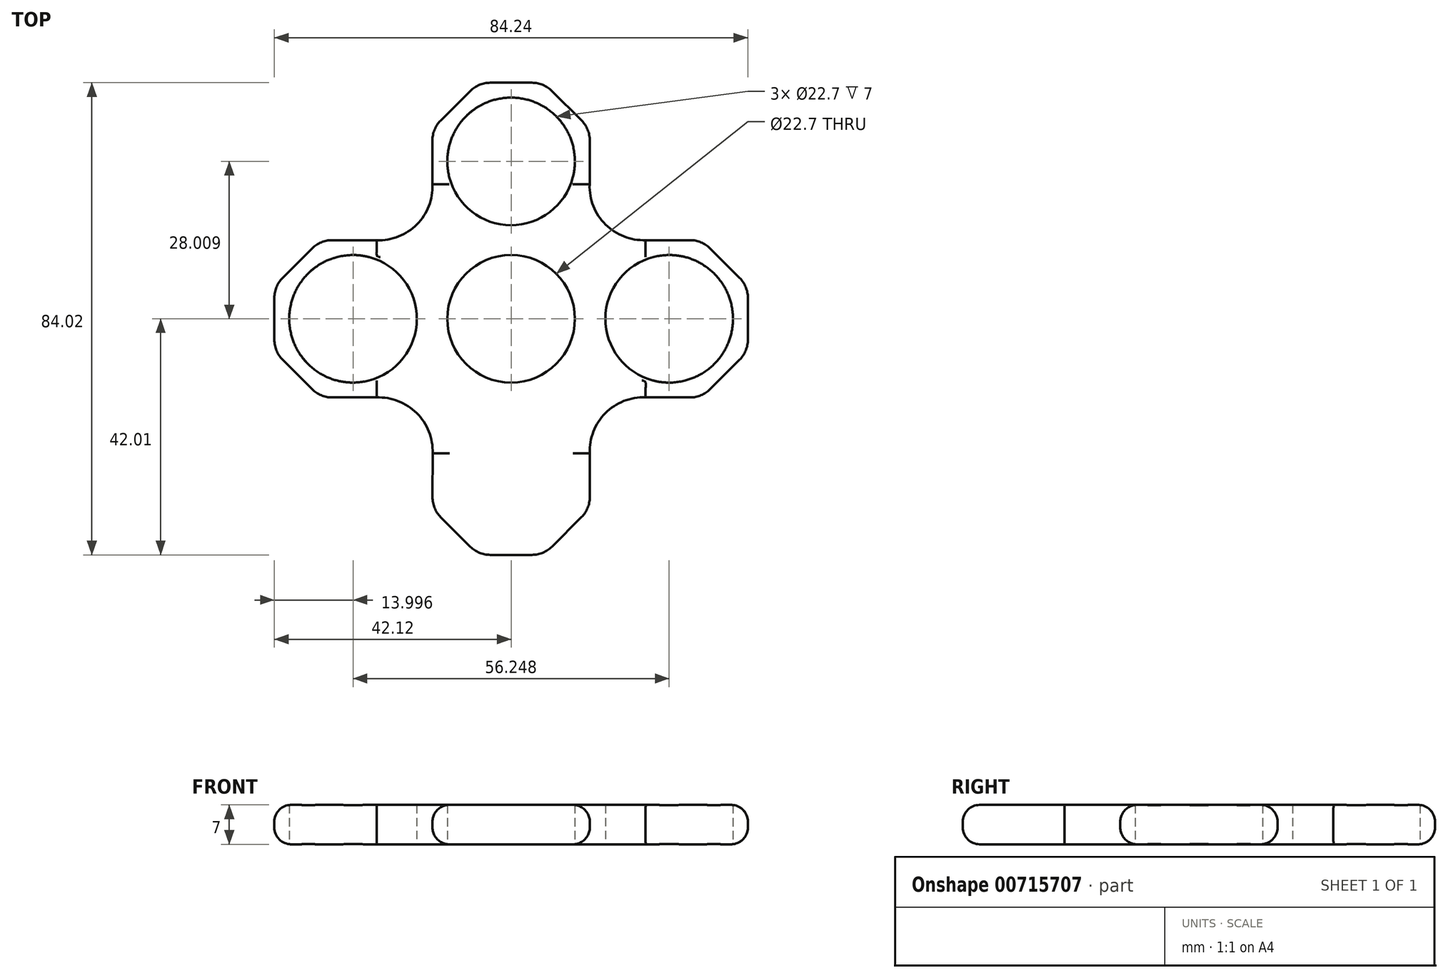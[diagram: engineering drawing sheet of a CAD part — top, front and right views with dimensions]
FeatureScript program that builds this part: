
annotation { "Feature Type Name" : "Feature", "Feature Type Description" : "" }
export const myFeature = defineFeature(function(context is Context, id is Id, definition is map)
    precondition{}
    {
        {
            var Q0;
            Q0=qCreatedBy(makeId("Top.planeOp"),FACE);
            var sketch = newSketch(context, id + "F0", { "sketchPlane" : qUnion([Q0])});
            skCircle(sketch, "E0", {"center": v(0, 0) * mm, "radius": 11.35 * mm});
            skCircle(sketch, "E1", {"center": v(28.12, 0) * mm, "radius": 11.35 * mm});
            skLineSegment(sketch, "E2.1", {"start": v(35.39, 12.54) * mm, "end": v(40.66, 7.26) * mm});
            skLineSegment(sketch, "E2.2", {"start": v(42.12, 3.73) * mm, "end": v(42.12, -3.73) * mm});
            skLineSegment(sketch, "E3.MirrorCS", {"start": v(-42.12, 3.73) * mm, "end": v(-42.12, -3.73) * mm});
            skLineSegment(sketch, "E4.MirrorCS", {"start": v(-40.66, -7.26) * mm, "end": v(-35.39, -12.54) * mm});
            skCircle(sketch, "E5.MirrorC", {"center": v(-28.12, 0) * mm, "radius": 11.35 * mm});
            skCircle(sketch, "E6", {"center": v(0, 28) * mm, "radius": 11.35 * mm});
            skLineSegment(sketch, "E7.0", {"start": v(-3.73, 42) * mm, "end": v(3.73, 42) * mm});
            skLineSegment(sketch, "E7.7", {"start": v(-12.54, 35.27) * mm, "end": v(-7.26, 40.54) * mm});
            skCircle(sketch, "E8.MirrorC", {"center": v(0, -28) * mm, "radius": 11.35 * mm});
            skLineSegment(sketch, "E9.MirrorCS", {"start": v(7.26, -40.54) * mm, "end": v(12.54, -35.27) * mm});
            skLineSegment(sketch, "E10.MirrorCS", {"start": v(-3.73, -42) * mm, "end": v(3.73, -42) * mm});
            skLineSegment(sketch, "E11", {"start": v(-35.4, 12.53) * mm, "end": v(-40.66, 7.26) * mm});
            skLineSegment(sketch, "E12", {"start": v(7.26, 40.54) * mm, "end": v(12.53, 35.28) * mm});
            skLineSegment(sketch, "E13", {"start": v(40.66, -7.26) * mm, "end": v(35.4, -12.53) * mm});
            skLineSegment(sketch, "E14", {"start": v(-7.26, -40.54) * mm, "end": v(-12.53, -35.28) * mm});
            skArc(sketch, "E15", {"start": v(13.97, 23.9) * mm, "mid": v(16.8, 16.78) * mm, "end": v(23.93, 14) * mm});
            skArc(sketch, "E16.1.0", {"start": v(-23.9, 13.97) * mm, "mid": v(-16.78, 16.8) * mm, "end": v(-14, 23.93) * mm});
            skArc(sketch, "E16.2.0", {"start": v(-13.97, -23.9) * mm, "mid": v(-16.8, -16.78) * mm, "end": v(-23.93, -14) * mm});
            skArc(sketch, "E16.3.0", {"start": v(23.9, -13.97) * mm, "mid": v(16.78, -16.8) * mm, "end": v(14, -23.93) * mm});
            skLineSegment(sketch, "E17", {"start": v(-14, 31.74) * mm, "end": v(-14, 23.93) * mm});
            skLineSegment(sketch, "E18", {"start": v(14, 31.73) * mm, "end": v(13.97, 23.9) * mm});
            skLineSegment(sketch, "E19", {"start": v(31.85, 14) * mm, "end": v(23.93, 14) * mm});
            skLineSegment(sketch, "E20", {"start": v(31.84, -14) * mm, "end": v(23.9, -13.97) * mm});
            skLineSegment(sketch, "E21", {"start": v(14, -23.93) * mm, "end": v(14, -31.74) * mm});
            skLineSegment(sketch, "E22", {"start": v(-14, -31.73) * mm, "end": v(-13.97, -23.9) * mm});
            skLineSegment(sketch, "E23", {"start": v(-23.93, -14) * mm, "end": v(-31.85, -14) * mm});
            skLineSegment(sketch, "E24", {"start": v(-31.84, 14) * mm, "end": v(-23.9, 13.97) * mm});
            skPoint(sketch, "E25.visualSharp", {"position": v(-5.8, 42) * mm});
            skArc(sketch, "E25.filletArc", {"start": v(-3.73, 42) * mm, "mid": v(-5.64, 41.63) * mm, "end": v(-7.26, 40.54) * mm});
            skPoint(sketch, "E26.visualSharp", {"position": v(5.8, 42) * mm});
            skArc(sketch, "E26.filletArc", {"start": v(7.26, 40.54) * mm, "mid": v(5.64, 41.63) * mm, "end": v(3.73, 42) * mm});
            skPoint(sketch, "E27.visualSharp", {"position": v(14, 33.8) * mm});
            skArc(sketch, "E27.filletArc", {"start": v(14, 31.73) * mm, "mid": v(13.62, 33.65) * mm, "end": v(12.53, 35.28) * mm});
            skPoint(sketch, "E28.visualSharp", {"position": v(-14, 33.8) * mm});
            skArc(sketch, "E28.filletArc", {"start": v(-12.54, 35.27) * mm, "mid": v(-13.62, 33.65) * mm, "end": v(-14, 31.74) * mm});
            skPoint(sketch, "E29.visualSharp", {"position": v(42.12, 5.8) * mm});
            skArc(sketch, "E29.filletArc", {"start": v(42.12, 3.73) * mm, "mid": v(41.74, 5.64) * mm, "end": v(40.66, 7.26) * mm});
            skPoint(sketch, "E30.visualSharp", {"position": v(42.12, -5.8) * mm});
            skArc(sketch, "E30.filletArc", {"start": v(40.66, -7.26) * mm, "mid": v(41.74, -5.64) * mm, "end": v(42.12, -3.73) * mm});
            skPoint(sketch, "E31.visualSharp", {"position": v(33.92, -14) * mm});
            skArc(sketch, "E31.filletArc", {"start": v(31.84, -14) * mm, "mid": v(33.76, -13.62) * mm, "end": v(35.4, -12.53) * mm});
            skPoint(sketch, "E32.visualSharp", {"position": v(33.92, 14) * mm});
            skArc(sketch, "E32.filletArc", {"start": v(35.39, 12.54) * mm, "mid": v(33.77, 13.62) * mm, "end": v(31.85, 14) * mm});
            skPoint(sketch, "E33.visualSharp", {"position": v(14, -33.8) * mm});
            skArc(sketch, "E33.filletArc", {"start": v(12.54, -35.27) * mm, "mid": v(13.62, -33.65) * mm, "end": v(14, -31.74) * mm});
            skPoint(sketch, "E34.visualSharp", {"position": v(5.8, -42) * mm});
            skArc(sketch, "E34.filletArc", {"start": v(3.73, -42) * mm, "mid": v(5.64, -41.63) * mm, "end": v(7.26, -40.54) * mm});
            skPoint(sketch, "E35.visualSharp", {"position": v(-5.8, -42) * mm});
            skArc(sketch, "E35.filletArc", {"start": v(-7.26, -40.54) * mm, "mid": v(-5.64, -41.63) * mm, "end": v(-3.73, -42) * mm});
            skPoint(sketch, "E36.visualSharp", {"position": v(-14, -33.8) * mm});
            skArc(sketch, "E36.filletArc", {"start": v(-14, -31.73) * mm, "mid": v(-13.62, -33.65) * mm, "end": v(-12.53, -35.28) * mm});
            skPoint(sketch, "E37.visualSharp", {"position": v(-33.92, -14) * mm});
            skArc(sketch, "E37.filletArc", {"start": v(-35.39, -12.54) * mm, "mid": v(-33.77, -13.62) * mm, "end": v(-31.85, -14) * mm});
            skPoint(sketch, "E38.visualSharp", {"position": v(-42.12, -5.8) * mm});
            skArc(sketch, "E38.filletArc", {"start": v(-42.12, -3.73) * mm, "mid": v(-41.74, -5.64) * mm, "end": v(-40.66, -7.26) * mm});
            skPoint(sketch, "E39.visualSharp", {"position": v(-42.12, 5.8) * mm});
            skArc(sketch, "E39.filletArc", {"start": v(-40.66, 7.26) * mm, "mid": v(-41.74, 5.64) * mm, "end": v(-42.12, 3.73) * mm});
            skPoint(sketch, "E40.visualSharp", {"position": v(-33.92, 14) * mm});
            skArc(sketch, "E40.filletArc", {"start": v(-31.84, 14) * mm, "mid": v(-33.76, 13.62) * mm, "end": v(-35.4, 12.53) * mm});
            skSolve(sketch);
        }
        {
            var Q0;
            Q0=makeQuery(id+"F0.imprint","IMPRINT",FACE,{"disambiguationData":[TD([[makeQuery(id+"F0.imprint","IMPRINT",EDGE,{"derivedFrom":sQuery(id+"F0.wireOp",EDGE,"20f8a018-4772-4a44-850f-0ec9f51ec483.0")}),1.0]])]});
            var Q1;
            Q1=makeQuery(id+"F0.imprint","IMPRINT",FACE,{"disambiguationData":[TD([[makeQuery(id+"F0.imprint","IMPRINT",EDGE,{"derivedFrom":sQuery(id+"F0.wireOp",EDGE,"E0")}),-1.0]])]});
            var Q2;
            Q2=makeQuery(id+"F0.imprint","IMPRINT",FACE,{"disambiguationData":[TD([[makeQuery(id+"F0.imprint","IMPRINT",EDGE,{"derivedFrom":sQuery(id+"F0.wireOp",EDGE,"E6")}),-1.0]])]});
            var Q3;
            Q3=makeQuery(id+"F0.imprint","IMPRINT",FACE,{"disambiguationData":[TD([[makeQuery(id+"F0.imprint","IMPRINT",EDGE,{"derivedFrom":sQuery(id+"F0.wireOp",EDGE,"E1")}),-1.0]])]});
            var Q4;
            Q4=makeQuery(id+"F0.imprint","IMPRINT",FACE,{"disambiguationData":[TD([[makeQuery(id+"F0.imprint","IMPRINT",EDGE,{"derivedFrom":sQuery(id+"F0.wireOp",EDGE,"E8.MirrorC")}),1.0]])]});
            var Q5;
            {var subQ1=sQuery(id+"F0.wireOp",EDGE,"50dad3a2-19dd-4acd-850b-96a279a4583b0.MirrorCS");Q5=makeQuery(id+"F0.imprint","IMPRINT",FACE,{"disambiguationData":[TD([[makeQuery(id+"F0.imprint","IMPRINT",EDGE,{"derivedFrom":subQ1}),1.0]])]});}
            extrude(context, id + "F1", {"entities" : qUnion([Q0, Q1, Q2, Q3, Q4, Q5]), "depth" : 7 * mm, "offsetDistance" : 25 * mm});
        }
        {
            var Q0;
            Q0=makeQuery(id+"F1.opExtrude","SWEPT_FACE",FACE,{"disambiguationData":[OSD([sQuery(id+"F0.wireOp",EDGE,"E3.MirrorCS")])]});
            var Q1;
            Q1=makeQuery(id+"F1.opExtrude","SWEPT_FACE",FACE,{"disambiguationData":[OSD([sQuery(id+"F0.wireOp",EDGE,"E10.MirrorCS")])]});
            var Q2;
            Q2=makeQuery(id+"F1.opExtrude","SWEPT_FACE",FACE,{"disambiguationData":[OSD([sQuery(id+"F0.wireOp",EDGE,"E2.2")])]});
            var Q3;
            Q3=makeQuery(id+"F1.opExtrude","SWEPT_FACE",FACE,{"disambiguationData":[OSD([sQuery(id+"F0.wireOp",EDGE,"E7.0")])]});
            fillet(context, id + "F2", {"entities" : qUnion([Q0, Q1, Q2, Q3]), "radius" : 3 * mm, "tangentPropagation" : true, "allowEdgeOverflow" : false});
        }
    });
